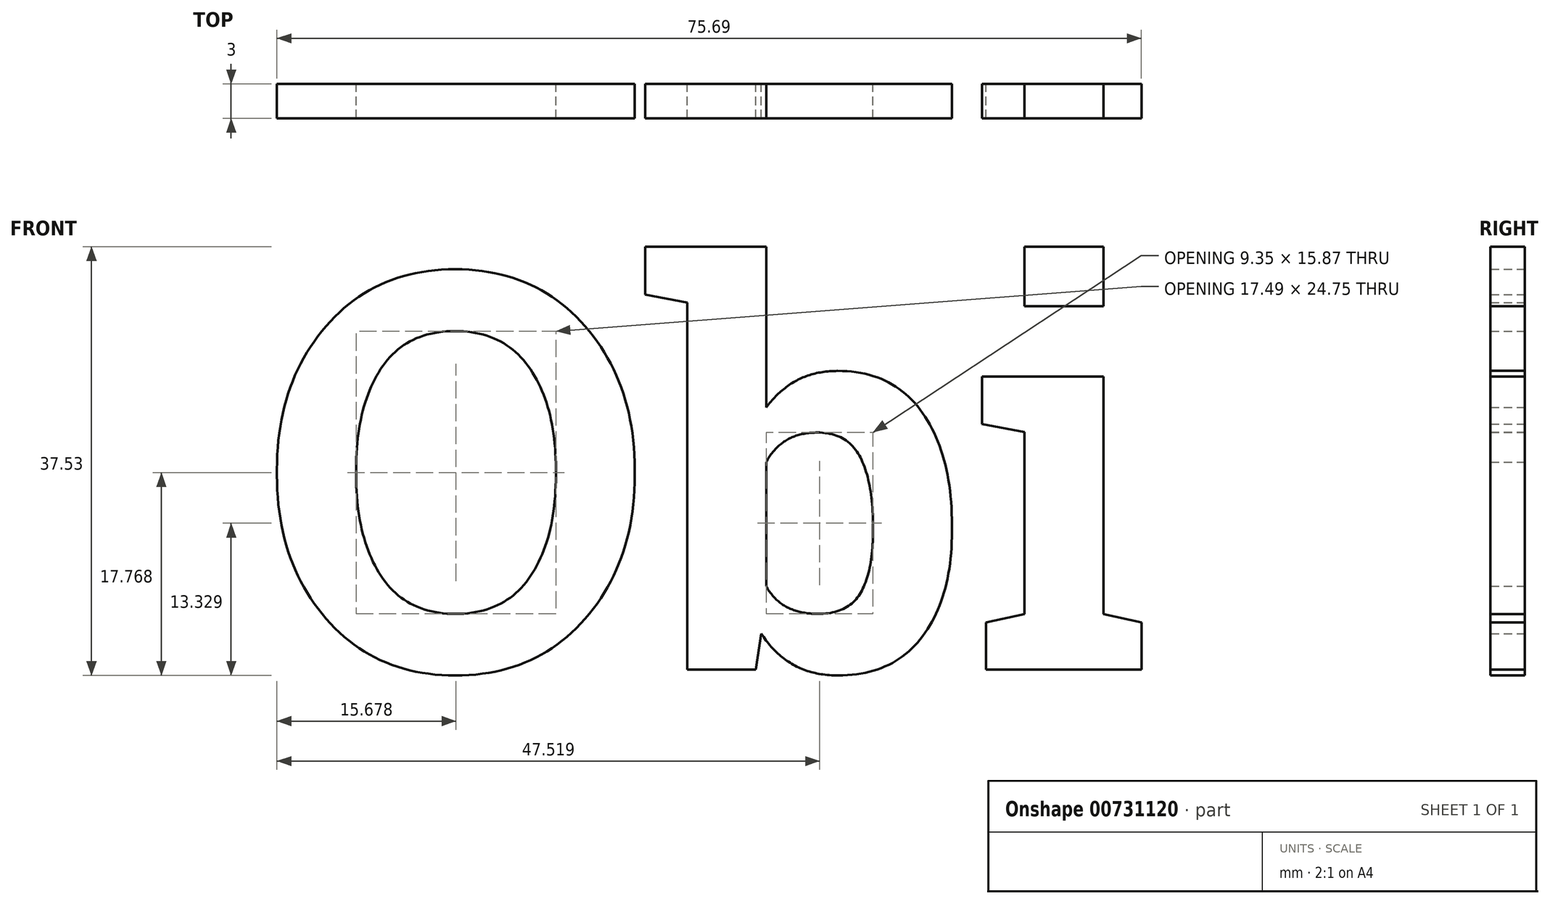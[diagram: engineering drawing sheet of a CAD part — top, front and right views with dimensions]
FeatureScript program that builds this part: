
annotation { "Feature Type Name" : "Feature", "Feature Type Description" : "" }
export const myFeature = defineFeature(function(context is Context, id is Id, definition is map)
    precondition{}
    {
        {
            var Q0;
            Q0=qCreatedBy(makeId("Front.planeOp"),FACE);
            var sketch = newSketch(context, id + "F0", { "sketchPlane" : qUnion([Q0])});
            skText(sketch, "E0", { "text": "Obi", "fontName": "RobotoSlab-Bold.ttf"});
            const initialGuessF0  = {"E0": [-0.03447, -0.00902, 1, 0, 0.035]};
            skSetInitialGuess(sketch, initialGuessF0);
            skSolve(sketch);
        }
        {
            var Q0;
            Q0 = qSketchRegion(id + "F0", true);
            extrude(context, id + "F1", {"entities" : qUnion([Q0]), "depth" : 3 * mm, "offsetDistance" : 25 * mm});
        }
    });
